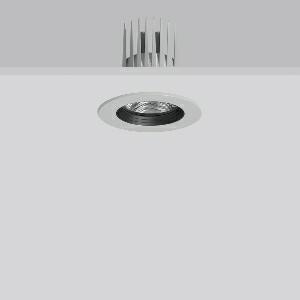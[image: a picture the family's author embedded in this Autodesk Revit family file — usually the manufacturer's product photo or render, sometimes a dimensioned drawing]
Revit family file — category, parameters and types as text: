
# Revit family: heledon_mini_e_901742_004_2_9ea1
name_source: partatom
category: Lighting Fixtures
units: mm (PartAtom-declared; Revit-internal decimal feet)

## family parameters
Cut with Voids When Loaded = No
Host = Face
Light Source = No
Part Type = Normal
Room Calculation Point = No
Round Connector Dimension = Use Diameter
Shared = No

## types (1)
- HELEDON mini E (1 x LED Modul 927, 2400 lm, 2700)
    Apparent Load = 20 VA
    Approval mark = CE
    CIE Flux Codes = 95 99 100 100 100
    Color Rendering = 92
    Color Temperature = 2700
    Default Elevation = 1800 mm
    Description = Series: HELEDON mini
Round recessed downlight. Housing: die-cast aluminium, powder-coated. Black plastic ring and recessed LED to prevent glare from the side. Optical assembly with reflector made of MIRO-Silver with 98% total light reflection for outstanding efficiency - can be changed without tools. Best colour rendering index Ra>90. Suitable for Recessed ceiling mounting. Installation without tools thanks to spring fastening system. Including separate LED converter with connecting cable 600 mm.High quality converter without flickering and stroboscopic effect. Through-wiring box (5 pole) available as accessory. The following accessories can be mounted without use of tools: interchangeable lenses, decorative glasses, honeycomb louvre, clear and frosted diffusers, white interchangeable plastic ring. 
Colour: silver
Diameter: 124 mm
Height: 3 mm
Cut-out diameter: 114 mm
Recess height: 170 mm
Luminaire: recess height: 120 mm
Lamp: LED
Socket: without socket
Colour temperature: 2700K
Colour rendering index (CRI): 92
System power: 20 W
Rated luminous flux: 2400 lm
Luminous efficiency: 120 lm/W
Control gear: Regulated power supply
Protection class: II
Type of protection: IP 20
    Height = 0 mm  [stored 0 ft]
    Lamp = 1 x LED Modul 927
    Lamp Light Flux = 2400 lm
    Lamp count = 1
    Length = 124 mm  [stored 0.406824 ft]
    Lifetime = 50000 h
    Luminous efficacy = 120 lm/W
    Manufacturer = RZB
    ModVariant = No
    Model = 901742.004.2
    Mounting Place = Ceiling
    Mounting Type = Recessed
    Number of Poles = 1
    OnlyDefault = Yes
    Power Factor = 1
    Product Name = HELEDON mini E
    Product group = Recessed downlights
    ProductGroupID = 402
    Protection Class = Protection class II
    Protection Degree = IP 20
    RLX_Detail_Level = 1
    RLX_Emergency_Light_Flux = 0 lm
    RLX_Emergency_Type = 0
    RLX_Emergency_Type_DB = No
    RlxData = <blob elided: 129001 chars, md5=91edefaa>
    Socket = socket
    Standby Power = 0 W
    System Light Flux = 2400 lm
    System Power = 20 W
    Type Comments = Product without accessories
    Type Image = 901657.004.jpg
    URL = http://relux.com
    VarID = ---
    Voltage = 230 V
    Voltage Range = 220-240 V
    Weight = 0.00 kg
    Width = 0 mm  [stored 0 ft]

note: [stored X ft] marks values corroborated as IEEE doubles in the binary element streams (Revit-internal decimal feet)

## geometry (parser evidence)
native form markers: Blend x4, Sweep x11
no freeform markers — native parametric forms only
